FCSTD DOCUMENT  (FreeCAD 0.19.4R1_voidlinux)
Label: asm_clock_hands
License: All rights reserved
LicenseURL: http://en.wikipedia.org/wiki/All_rights_reserved
objects: App::Link×5, App::DocumentObjectGroup×3, PartDesign::CoordinateSystem×1, App::FeaturePython×1, App::Part×1
note: 1 computed .brp shape members not serialized (recipe doc carries the construction recipe); baked Part::Feature solids carry a one-line shape summary decoded from their .brp
EXTERNAL_REF file=clock_face.FCStd obj=LCS_tophole
EXTERNAL_REF file=clock_face.FCStd obj=Part
EXTERNAL_REF file=hand_alarm.FCStd obj=LCS_tophole
EXTERNAL_REF file=hand_alarm.FCStd obj=Part
EXTERNAL_REF file=hand_hour.FCStd obj=LCS_tophole
EXTERNAL_REF file=hand_hour.FCStd obj=Part
EXTERNAL_REF file=hand_minute.FCStd obj=LCS_tophole
EXTERNAL_REF file=hand_minute.FCStd obj=Part
EXTERNAL_REF file=hand_seconds.FCStd obj=LCS_topcenter
EXTERNAL_REF file=hand_seconds.FCStd obj=Part

FEATURE [App::DocumentObjectGroup] Parts
FEATURE [PartDesign::CoordinateSystem] LCS_Origin
  AttacherType = Attacher::AttachEngine3D
  MapMode = 2
  Support = -> [X_Axis]
FEATURE [App::DocumentObjectGroup] Constraints
FEATURE [App::FeaturePython] Variables  # WARN: FeaturePython — macro-defined, semantics opaque (R4)
  Type = App::PropertyContainer
FEATURE [App::DocumentObjectGroup] Configurations
FEATURE [App::Link] clock_face
  AttachedBy = #LCS_tophole
  AttachedTo = Parent Assembly#LCS_Origin
  LinkPlacement = pos=(0,0,0) rot=(0,0,-1;1.5708rad)
  LinkedObject = -> <external clock_face.FCStd>#Part
  Placement = pos=(0,0,0) rot=(0,0,-1;1.5708rad)
  SolverId = Asm4EE
  expr: Placement = LCS_Origin.Placement * AttachmentOffset * clock_face#LCS_tophole.Placement ^ -1
FEATURE [App::Link] hand_alarm
  AttachedBy = #LCS_tophole
  AttachedTo = clock_face#LCS_tophole
  AttachmentOffset = pos=(0,0,1.3) rot=(0,0,1;0rad)
  LinkPlacement = pos=(0,0,1.3) rot=(0,0,1;1.0472rad)
  LinkedObject = -> <external hand_alarm.FCStd>#Part
  Placement = pos=(0,0,1.3) rot=(0,0,1;1.0472rad)
  SolverId = Asm4EE
  expr: Placement = clock_face.Placement * clock_face#LCS_tophole.Placement * AttachmentOffset * hand_alarm#LCS_tophole.Placement ^ -1
FEATURE [App::Link] hand_hour
  AttachedBy = #LCS_tophole
  AttachedTo = clock_face#LCS_tophole
  AttachmentOffset = pos=(0,0,2.6) rot=(0,0,1;0rad)
  LinkPlacement = pos=(0,0,2.6) rot=(0,0,1;2.0944rad)
  LinkedObject = -> <external hand_hour.FCStd>#Part
  Placement = pos=(0,0,2.6) rot=(0,0,1;2.0944rad)
  SolverId = Asm4EE
  expr: Placement = clock_face.Placement * clock_face#LCS_tophole.Placement * AttachmentOffset * hand_hour#LCS_tophole.Placement ^ -1
FEATURE [App::Link] hand_minute
  AttachedBy = #LCS_tophole
  AttachedTo = clock_face#LCS_tophole
  AttachmentOffset = pos=(0,0,3.9) rot=(0,0,1;0rad)
  LinkPlacement = pos=(0,0,3.9) rot=(0,0,1;0.349066rad)
  LinkedObject = -> <external hand_minute.FCStd>#Part
  Placement = pos=(0,0,3.9) rot=(0,0,1;0.349066rad)
  SolverId = Asm4EE
  expr: Placement = clock_face.Placement * clock_face#LCS_tophole.Placement * AttachmentOffset * hand_minute#LCS_tophole.Placement ^ -1
FEATURE [App::Link] hand_seconds
  AttachedBy = #LCS_topcenter
  AttachedTo = clock_face#LCS_tophole
  AttachmentOffset = pos=(0,0,5.5) rot=(0,0,1;0rad)
  LinkPlacement = pos=(8e-16,-5e-16,4.1) rot=(0,0,1;0rad)
  LinkedObject = -> <external hand_seconds.FCStd>#Part
  Placement = pos=(8e-16,-5e-16,4.1) rot=(0,0,1;0rad)
  SolverId = Asm4EE
  expr: Placement = clock_face.Placement * clock_face#LCS_tophole.Placement * AttachmentOffset * hand_seconds#LCS_topcenter.Placement ^ -1
FEATURE [App::Part] Model
  Group = -> [LCS_Origin,Constraints,Variables,Configurations,clock_face,hand_alarm,hand_hour,hand_minute,hand_seconds]
  Origin = -> Origin
  Type = Assembly

RESOLVED EXTERNAL PARTS (link-assembly join: the EXTERNAL_REF files above that resolve inside this repo's crawl, each included once):
---- part clock_face.FCStd = doc fcstd_eb16558f8f3e ----
FCSTD DOCUMENT  (FreeCAD 0.19.4R1_voidlinux)
Label: clock_face
License: All rights reserved
LicenseURL: http://en.wikipedia.org/wiki/All_rights_reserved
objects: Sketcher::SketchObject×2, PartDesign::Pad×1, PartDesign::Pocket×1, PartDesign::Body×1, PartDesign::CoordinateSystem×1, App::Part×1
note: 8 computed .brp shape members not serialized (recipe doc carries the construction recipe); baked Part::Feature solids carry a one-line shape summary decoded from their .brp
EXTERNAL_REF file=master_animator.FCStd obj=Variables

FEATURE [Sketcher::SketchObject] Sketch
  FullyConstrained = true
  MapMode = 5
  Support = -> [XY_Plane001]
  sketch-geometry (8):
    g0: LineSegment StartX=-26 StartY=22 StartZ=0 EndX=-26 EndY=-22 EndZ=0
    g1: LineSegment StartX=26 StartY=22 StartZ=0 EndX=26 EndY=-22 EndZ=0
    g2: LineSegment StartX=-22 StartY=26 StartZ=0 EndX=22 EndY=26 EndZ=0
    g3: LineSegment StartX=-22 StartY=-26 StartZ=0 EndX=22 EndY=-26 EndZ=0
    g4: ArcOfCircle CenterX=-22 CenterY=22 CenterZ=0 NormalX=0 NormalY=0 NormalZ=1 AngleXU=0 Radius=4 StartAngle=1.57079 EndAngle=3.1416
    g5: ArcOfCircle CenterX=22 CenterY=22 CenterZ=0 NormalX=0 NormalY=0 NormalZ=1 AngleXU=0 Radius=4.00002 StartAngle=1.95399e-08 EndAngle=1.5708
    g6: ArcOfCircle CenterX=22 CenterY=-22 CenterZ=0 NormalX=0 NormalY=0 NormalZ=1 AngleXU=0 Radius=4.00002 StartAngle=4.71239 EndAngle=6.28319
    g7: ArcOfCircle CenterX=-22 CenterY=-22 CenterZ=0 NormalX=0 NormalY=0 NormalZ=1 AngleXU=0 Radius=4.00002 StartAngle=3.14159 EndAngle=4.71239
  constraints (22):
    c: Coincident(g4,g2)
    c: Coincident(g4,g0)
    c: Coincident(g5,g1)
    c: Coincident(g5,g2)
    c: Coincident(g6,g1)
    c: Coincident(g6,g3)
    c: Coincident(g7,g0)
    c: Coincident(g7,g3)
    c: Symmetric(g1,g0,g-2)
    c: Symmetric(g2,g2,g-2)
    c: Symmetric(g0,g0,g-1)
    c: Symmetric(g2,g3,g-1)
    c: Symmetric(g3,g2,g-1)
    c: Symmetric(g1,g0,g-1)
    c: Tangent(g4,g2)
    c: Tangent(g4,g0)
    c: Tangent(g0,g7)
    c: Tangent(g3,g6)
    c: Tangent(g1,g5)
    c: DistanceY(g3,g2) = 52
    c: Equal(g0,g2)
    c: Radius(g4) = 4
FEATURE [PartDesign::Pad] Pad
  Direction = (1,1,1)
  Length = 1
  Length2 = 100
  Profile = -> Sketch
  Reversed = true
  Type = 0
FEATURE [Sketcher::SketchObject] Sketch001
  FullyConstrained = true
  MapMode = 5
  Support = -> [Pad]
  sketch-geometry (1):
    g0: Circle CenterX=0 CenterY=0 CenterZ=0 NormalX=0 NormalY=0 NormalZ=1 AngleXU=0 Radius=3
  constraints (2):
    c: Coincident(g0,g-1)
    c: Radius(g0) = 3
FEATURE [PartDesign::Pocket] Pocket
  BaseFeature = -> Pad
  Length = 5
  Length2 = 100
  Profile = -> Sketch001
  Type = 1
FEATURE [PartDesign::Body] Body
  Group = -> [Sketch,Pad,Sketch001,Pocket]
  Origin = -> Origin001
  Tip = -> Pocket
FEATURE [PartDesign::CoordinateSystem] LCS_tophole
  AttacherType = Attacher::AttachEngine3D
  MapMode = 11
  Placement = pos=(0,0,0) rot=(0,0,1;1.5708rad)
  Support = -> [Pocket]
  expr: .AttachmentOffset.Base.z = -master_animator#Variables.explode * 3
FEATURE [App::Part] Part  label="clock_face"
  Group = -> [LCS_tophole,Body]
  Origin = -> Origin
---- part hand_alarm.FCStd = doc fcstd_c77f37d60b10 ----
FCSTD DOCUMENT  (FreeCAD 0.19.4R1_voidlinux)
Label: hand_alarm
License: All rights reserved
LicenseURL: http://en.wikipedia.org/wiki/All_rights_reserved
objects: Sketcher::SketchObject×2, PartDesign::Revolution×1, PartDesign::Pocket×1, PartDesign::Body×1, PartDesign::CoordinateSystem×1, App::Part×1
note: 8 computed .brp shape members not serialized (recipe doc carries the construction recipe); baked Part::Feature solids carry a one-line shape summary decoded from their .brp
EXTERNAL_REF file=master_animator.FCStd obj=Variables

FEATURE [Sketcher::SketchObject] Sketch
  FullyConstrained = true
  MapMode = 5
  Placement = pos=(0,0,0) rot=(0.57735,0.57735,0.57735;2.0944rad)
  Support = -> [YZ_Plane001]
  sketch-geometry (6):
    g0: LineSegment StartX=-14 StartY=0 StartZ=0 EndX=-14 EndY=-1 EndZ=0
    g1: LineSegment StartX=-14 StartY=-1 StartZ=0 EndX=-2.8 EndY=-1 EndZ=0
    g2: LineSegment StartX=-2.8 StartY=-1 StartZ=0 EndX=-2.8 EndY=-5 EndZ=0
    g3: LineSegment StartX=-2.8 StartY=-5 StartZ=0 EndX=-2.3 EndY=-5 EndZ=0
    g4: LineSegment StartX=-2.3 StartY=-5 StartZ=0 EndX=-2.3 EndY=0 EndZ=0
    g5: LineSegment StartX=-14 StartY=0 StartZ=0 EndX=-2.3 EndY=0 EndZ=0
  constraints (18):
    c: PointOnObject(g0,g-1)
    c: Vertical(g0)
    c: Coincident(g1,g0)
    c: Horizontal(g1)
    c: Coincident(g2,g1)
    c: Vertical(g2)
    c: Coincident(g3,g2)
    c: Horizontal(g3)
    c: Coincident(g4,g3)
    c: Vertical(g4)
    c: PointOnObject(g4,g-1)
    c: Coincident(g5,g0)
    c: Coincident(g5,g4)
    c: Distance(g3) = 0.5
    c: DistanceX(g-2,g2) = -2.8
    c: DistanceX(g-2,g0) = -14
    c: Distance(g4) = 5
    c: Distance(g0) = 1
FEATURE [PartDesign::Revolution] Revolution
  Angle = 360
  Axis = (-2e-16,3e-16,1)
  Base = (0,0,0)
  Placement = pos=(0,0,0) rot=(0.57735,0.57735,0.57735;2.0944rad)
  Profile = -> Sketch
  ReferenceAxis = -> Sketch [V_Axis]
FEATURE [Sketcher::SketchObject] Sketch001
  ExternalGeometry = -> [Revolution]
  FullyConstrained = true
  MapMode = 5
  Placement = pos=(0,0,2.3e-15) rot=(0,0,-1;1.5708rad)
  Support = -> [Revolution]
  sketch-geometry (6):
    g0: LineSegment StartX=-13.9943 StartY=0.4 StartZ=0 EndX=-3.4641 EndY=0.5 EndZ=0
    g1: LineSegment StartX=-3.4641 StartY=-0.5 StartZ=0 EndX=-13.9943 EndY=-0.4 EndZ=0
    g2: ArcOfCircle CenterX=-2e-16 CenterY=9e-15 CenterZ=0 NormalX=0 NormalY=0 NormalZ=1 AngleXU=0 Radius=14 StartAngle=3.17017 EndAngle=9.3962
    g3: ArcOfCircle CenterX=-2e-16 CenterY=9e-15 CenterZ=0 NormalX=0 NormalY=0 NormalZ=1 AngleXU=0 Radius=3.5 StartAngle=3.28494 EndAngle=9.28143
    g4: LineSegment StartX=-3.4641 StartY=0.5 StartZ=0 EndX=-3.4641 EndY=0 EndZ=0
    g5: LineSegment StartX=-3.4641 StartY=0 StartZ=0 EndX=-3.4641 EndY=-0.5 EndZ=0
  constraints (17):
    c: PointOnObject(g0,g-3)
    c: Symmetric(g0,g1,g-1)
    c: DistanceY(g1,g0) = 1
    c: Coincident(g2,g0)
    c: Coincident(g2,g1)
    c: Coincident(g3,g2)
    c: Coincident(g3,g0)
    c: Radius(g3) = 3.5
    c: Equal(g2,g-3)
    c: DistanceY(g1,g0) = 0.8
    c: Coincident(g3,g1)
    c: Coincident(g4,g0)
    c: PointOnObject(g4,g-1)
    c: Vertical(g4)
    c: Coincident(g5,g4)
    c: Coincident(g5,g1)
    c: Vertical(g5)
FEATURE [PartDesign::Pocket] Pocket
  BaseFeature = -> Revolution
  Length = 5
  Length2 = 100
  Placement = pos=(0,0,0) rot=(0.57735,0.57735,0.57735;2.0944rad)
  Profile = -> Sketch001
  Type = 1
FEATURE [PartDesign::Body] Body
  Group = -> [Sketch,Revolution,Sketch001,Pocket]
  Origin = -> Origin001
  Tip = -> Pocket
FEATURE [PartDesign::CoordinateSystem] LCS_tophole
  AttacherType = Attacher::AttachEngine3D
  AttachmentOffset = pos=(0,0,0) rot=(0,0,-1;1.0472rad)
  MapMode = 11
  Placement = pos=(0,0,4e-16) rot=(0,0,-1;1.0472rad)
  Support = -> [Pocket]
  expr: .AttachmentOffset.Base.z = -master_animator#Variables.explode * 4
FEATURE [App::Part] Part  label="hand_alarm"
  Group = -> [LCS_tophole,Body]
  Origin = -> Origin
---- part hand_hour.FCStd = doc fcstd_4f2025e096bf ----
FCSTD DOCUMENT  (FreeCAD 0.19.4R1_voidlinux)
Label: hand_hour
License: All rights reserved
LicenseURL: http://en.wikipedia.org/wiki/All_rights_reserved
objects: Sketcher::SketchObject×3, PartDesign::Revolution×1, PartDesign::Pad×1, PartDesign::Pocket×1, PartDesign::Body×1, PartDesign::CoordinateSystem×1, App::Part×1
note: 11 computed .brp shape members not serialized (recipe doc carries the construction recipe); baked Part::Feature solids carry a one-line shape summary decoded from their .brp
EXTERNAL_REF file=master_animator.FCStd obj=Variables

FEATURE [Sketcher::SketchObject] Sketch
  FullyConstrained = true
  MapMode = 5
  Placement = pos=(0,0,0) rot=(0.57735,0.57735,0.57735;2.0944rad)
  Support = -> [YZ_Plane001]
  sketch-geometry (6):
    g0: LineSegment StartX=-3.3 StartY=0 StartZ=0 EndX=-1.7 EndY=0 EndZ=0
    g1: LineSegment StartX=-1.7 StartY=0 StartZ=0 EndX=-1.7 EndY=-7 EndZ=0
    g2: LineSegment StartX=-1.7 StartY=-7 StartZ=0 EndX=-2.2 EndY=-7 EndZ=0
    g3: LineSegment StartX=-2.2 StartY=-7 StartZ=0 EndX=-2.2 EndY=-1 EndZ=0
    g4: LineSegment StartX=-2.2 StartY=-1 StartZ=0 EndX=-3.3 EndY=-1 EndZ=0
    g5: LineSegment StartX=-3.3 StartY=0 StartZ=0 EndX=-3.3 EndY=-1 EndZ=0
  constraints (18):
    c: PointOnObject(g0,g-1)
    c: PointOnObject(g0,g-1)
    c: Coincident(g1,g0)
    c: Vertical(g1)
    c: Coincident(g2,g1)
    c: Horizontal(g2)
    c: Coincident(g3,g2)
    c: Vertical(g3)
    c: Coincident(g4,g3)
    c: Horizontal(g4)
    c: Coincident(g5,g0)
    c: Coincident(g5,g4)
    c: Vertical(g5)
    c: Distance(g5) = 1
    c: Distance(g2) = 0.5
    c: Distance(g1) = 7
    c: DistanceX(g0,g-1) = 3.3
    c: DistanceX(g2,g-1) = 2.2
FEATURE [PartDesign::Revolution] Revolution
  Angle = 360
  Axis = (-2e-16,3e-16,1)
  Base = (0,0,0)
  Placement = pos=(0,0,0) rot=(0.57735,0.57735,0.57735;2.0944rad)
  Profile = -> Sketch
  ReferenceAxis = -> Sketch [V_Axis]
FEATURE [Sketcher::SketchObject] Sketch001
  ExternalGeometry = -> [Revolution]
  FullyConstrained = true
  MapMode = 5
  Placement = pos=(0,0,5e-16) rot=(0,0,-1;1.5708rad)
  Support = -> [Revolution]
  sketch-geometry (5):
    g0: LineSegment StartX=3.10232 StartY=1.125 StartZ=0 EndX=3.10232 EndY=-1.125 EndZ=0
    g1: LineSegment StartX=3.10232 StartY=1.125 StartZ=0 EndX=17.009 EndY=1 EndZ=0
    g2: LineSegment StartX=3.10232 StartY=-1.125 StartZ=0 EndX=17.009 EndY=-1 EndZ=0
    g3: ArcOfCircle CenterX=17 CenterY=0 CenterZ=0 NormalX=0 NormalY=0 NormalZ=1 AngleXU=0 Radius=1.00004 StartAngle=4.72138 EndAngle=7.84499
    g4: GeomPoint X=16 Y=0 Z=0
  constraints (13):
    c: PointOnObject(g0,g-3)
    c: Symmetric(g0,g0,g-1)
    c: Coincident(g1,g0)
    c: Coincident(g2,g0)
    c: Symmetric(g1,g2,g-1)
    c: DistanceY(g2,g1) = 2
    c: DistanceY(g0,g0) = 2.25
    c: Coincident(g3,g1)
    c: Coincident(g3,g2)
    c: Tangent(g3,g1)
    c: PointOnObject(g4,g3)
    c: PointOnObject(g4,g-1)
    c: Distance(g-1,g4) = 16
FEATURE [PartDesign::Pad] Pad
  BaseFeature = -> Revolution
  Direction = (1,1,1)
  Length = 1
  Length2 = 100
  Placement = pos=(0,0,0) rot=(0.57735,0.57735,0.57735;2.0944rad)
  Profile = -> Sketch001
  Reversed = true
  Type = 0
FEATURE [Sketcher::SketchObject] Sketch002
  ExternalGeometry = -> [Pad]
  FullyConstrained = true
  MapMode = 5
  Placement = pos=(0,0,5e-16) rot=(0,0,-1;1.5708rad)
  Support = -> [Pad]
  sketch-geometry (7):
    g0: ArcOfCircle CenterX=11.5751 CenterY=0 CenterZ=0 NormalX=0 NormalY=0 NormalZ=1 AngleXU=0 Radius=0.575 StartAngle=1.5708 EndAngle=4.71239
    g1: ArcOfCircle CenterX=15.4251 CenterY=0 CenterZ=0 NormalX=0 NormalY=0 NormalZ=1 AngleXU=0 Radius=0.575 StartAngle=4.71239 EndAngle=7.85398
    g2: LineSegment StartX=11.5751 StartY=-0.575 StartZ=0 EndX=15.4251 EndY=-0.575 EndZ=0
    g3: LineSegment StartX=11.5751 StartY=0.575 StartZ=0 EndX=15.4251 EndY=0.575 EndZ=0
    g4: GeomPoint X=11.0001 Y=0 Z=0
    g5: GeomPoint X=16.0001 Y=0 Z=0
    g6: GeomPoint X=18.0001 Y=0 Z=0
  constraints (16):
    c: Tangent(g0,g3) = 1.5708
    c: Tangent(g0,g2) = -1.5708
    c: Tangent(g2,g1) = -1.5708
    c: Tangent(g3,g1) = 1.5708
    c: Horizontal(g2)
    c: Equal(g0,g1)
    c: PointOnObject(g0,g-1)
    c: PointOnObject(g4,g0)
    c: PointOnObject(g5,g1)
    c: PointOnObject(g4,g-1)
    c: PointOnObject(g5,g-1)
    c: Distance(g4,g5) = 5
    c: Distance(g0,g0) = 1.15
    c: PointOnObject(g6,g-3)
    c: PointOnObject(g6,g-1)
    c: Distance(g5,g6) = 2
FEATURE [PartDesign::Pocket] Pocket
  BaseFeature = -> Pad
  Length = 0.1
  Length2 = 100
  Placement = pos=(0,0,0) rot=(0.57735,0.57735,0.57735;2.0944rad)
  Profile = -> Sketch002
  Type = 0
FEATURE [PartDesign::Body] Body
  Group = -> [Sketch,Revolution,Sketch001,Pad,Sketch002,Pocket]
  Origin = -> Origin001
  Tip = -> Pocket
FEATURE [PartDesign::CoordinateSystem] LCS_tophole
  AttacherType = Attacher::AttachEngine3D
  AttachmentOffset = pos=(0,0,0) rot=(0,0,-1;2.0944rad)
  MapMode = 11
  Placement = pos=(0,0,3e-16) rot=(0,0,-1;2.0944rad)
  Support = -> [Pocket]
  expr: .AttachmentOffset.Base.z = -master_animator#Variables.explode * 5
FEATURE [App::Part] Part  label="hand_hour"
  Group = -> [LCS_tophole,Body]
  Origin = -> Origin
---- part hand_minute.FCStd = doc fcstd_699d8df3e5ea ----
FCSTD DOCUMENT  (FreeCAD 0.19.4R1_voidlinux)
Label: hand_minute
License: All rights reserved
LicenseURL: http://en.wikipedia.org/wiki/All_rights_reserved
objects: Sketcher::SketchObject×3, PartDesign::Revolution×1, PartDesign::Pad×1, PartDesign::Pocket×1, PartDesign::Body×1, PartDesign::CoordinateSystem×1, App::Part×1
note: 11 computed .brp shape members not serialized (recipe doc carries the construction recipe); baked Part::Feature solids carry a one-line shape summary decoded from their .brp
EXTERNAL_REF file=master_animator.FCStd obj=Variables

FEATURE [Sketcher::SketchObject] Sketch
  FullyConstrained = true
  MapMode = 5
  Placement = pos=(0,0,0) rot=(0.57735,0.57735,0.57735;2.0944rad)
  Support = -> [YZ_Plane001]
  sketch-geometry (6):
    g0: LineSegment StartX=-3 StartY=0 StartZ=0 EndX=-1.1 EndY=0 EndZ=0
    g1: LineSegment StartX=-1.1 StartY=0 StartZ=0 EndX=-1.1 EndY=-9 EndZ=0
    g2: LineSegment StartX=-1.1 StartY=-9 StartZ=0 EndX=-1.6 EndY=-9 EndZ=0
    g3: LineSegment StartX=-1.6 StartY=-9 StartZ=0 EndX=-1.6 EndY=-1 EndZ=0
    g4: LineSegment StartX=-1.6 StartY=-1 StartZ=0 EndX=-3 EndY=-1 EndZ=0
    g5: LineSegment StartX=-3 StartY=-1 StartZ=0 EndX=-3 EndY=0 EndZ=0
  constraints (18):
    c: PointOnObject(g0,g-1)
    c: PointOnObject(g0,g-1)
    c: Coincident(g1,g0)
    c: Vertical(g1)
    c: Coincident(g2,g1)
    c: Horizontal(g2)
    c: Coincident(g3,g2)
    c: Vertical(g3)
    c: Coincident(g4,g3)
    c: Horizontal(g4)
    c: Coincident(g5,g4)
    c: Coincident(g5,g0)
    c: Vertical(g5)
    c: Distance(g2) = 0.5
    c: Distance(g0,g1) = 9
    c: Distance(g5) = 1
    c: Distance(g-1,g0) = 3
    c: DistanceX(g-2,g2) = -1.6
FEATURE [PartDesign::Revolution] Revolution
  Angle = 360
  Axis = (-2e-16,3e-16,1)
  Base = (0,0,0)
  Placement = pos=(0,0,0) rot=(0.57735,0.57735,0.57735;2.0944rad)
  Profile = -> Sketch
  ReferenceAxis = -> Sketch [V_Axis]
FEATURE [Sketcher::SketchObject] Sketch001
  ExternalGeometry = -> [Revolution]
  FullyConstrained = true
  MapMode = 5
  Placement = pos=(0,0,5e-16) rot=(0,0,-1;1.5708rad)
  Support = -> [Revolution]
  sketch-geometry (5):
    g0: LineSegment StartX=2.78107 StartY=1.125 StartZ=0 EndX=2.78107 EndY=-1.125 EndZ=0
    g1: LineSegment StartX=2.78107 StartY=1.125 StartZ=0 EndX=20.507 EndY=1 EndZ=0
    g2: LineSegment StartX=2.78107 StartY=-1.125 StartZ=0 EndX=20.507 EndY=-1 EndZ=0
    g3: ArcOfCircle CenterX=20.5 CenterY=0 CenterZ=0 NormalX=0 NormalY=0 NormalZ=1 AngleXU=0 Radius=1.00002 StartAngle=4.71944 EndAngle=7.84694
    g4: GeomPoint X=21.5 Y=0 Z=0
  constraints (13):
    c: PointOnObject(g0,g-3)
    c: Symmetric(g0,g0,g-1)
    c: Distance(g0) = 2.25
    c: Coincident(g1,g0)
    c: Coincident(g2,g0)
    c: Symmetric(g1,g2,g-1)
    c: Distance(g1,g2) = 2
    c: Coincident(g3,g1)
    c: Coincident(g3,g2)
    c: Tangent(g3,g1)
    c: PointOnObject(g4,g3)
    c: PointOnObject(g4,g-1)
    c: Distance(g-1,g4) = 21.5
FEATURE [PartDesign::Pad] Pad
  BaseFeature = -> Revolution
  Direction = (1,1,1)
  Length = 1
  Length2 = 100
  Placement = pos=(0,0,0) rot=(0.57735,0.57735,0.57735;2.0944rad)
  Profile = -> Sketch001
  Reversed = true
  Type = 0
FEATURE [Sketcher::SketchObject] Sketch002
  ExternalGeometry = -> [Pad]
  FullyConstrained = true
  MapMode = 5
  Placement = pos=(0,0,5e-16) rot=(0,0,-1;1.5708rad)
  Support = -> [Pad]
  sketch-geometry (7):
    g0: ArcOfCircle CenterX=12 CenterY=0 CenterZ=0 NormalX=0 NormalY=0 NormalZ=1 AngleXU=0 Radius=0.5 StartAngle=1.5708 EndAngle=4.71239
    g1: ArcOfCircle CenterX=18 CenterY=0 CenterZ=0 NormalX=0 NormalY=0 NormalZ=1 AngleXU=0 Radius=0.5 StartAngle=4.71239 EndAngle=7.85398
    g2: LineSegment StartX=12 StartY=-0.5 StartZ=0 EndX=18 EndY=-0.5 EndZ=0
    g3: LineSegment StartX=12 StartY=0.5 StartZ=0 EndX=18 EndY=0.5 EndZ=0
    g4: GeomPoint X=21.5 Y=0 Z=0
    g5: GeomPoint X=18.5 Y=0 Z=0
    g6: GeomPoint X=11.5 Y=0 Z=0
  constraints (16):
    c: Tangent(g0,g3) = 1.5708
    c: Tangent(g0,g2) = -1.5708
    c: Tangent(g2,g1) = -1.5708
    c: Tangent(g3,g1) = 1.5708
    c: Horizontal(g2)
    c: Equal(g0,g1)
    c: PointOnObject(g0,g-1)
    c: PointOnObject(g4,g-3)
    c: PointOnObject(g4,g-1)
    c: PointOnObject(g5,g1)
    c: PointOnObject(g5,g-1)
    c: Distance(g5,g4) = 3
    c: PointOnObject(g6,g0)
    c: PointOnObject(g6,g-1)
    c: Distance(g6,g5) = 7
    c: Distance(g0,g0) = 1
FEATURE [PartDesign::Pocket] Pocket
  BaseFeature = -> Pad
  Length = 0.1
  Length2 = 100
  Placement = pos=(0,0,0) rot=(0.57735,0.57735,0.57735;2.0944rad)
  Profile = -> Sketch002
  Type = 0
FEATURE [PartDesign::Body] Body
  Group = -> [Sketch,Revolution,Sketch001,Pad,Sketch002,Pocket]
  Origin = -> Origin001
  Tip = -> Pocket
FEATURE [PartDesign::CoordinateSystem] LCS_tophole
  AttacherType = Attacher::AttachEngine3D
  AttachmentOffset = pos=(0,0,0) rot=(0,0,-1;0.349066rad)
  MapMode = 11
  Placement = pos=(0,0,2e-16) rot=(0,0,-1;0.349066rad)
  Support = -> [Pocket]
  expr: .AttachmentOffset.Base.z = -master_animator#Variables.explode * 6
FEATURE [App::Part] Part  label="hand_minute"
  Group = -> [LCS_tophole,Body]
  Origin = -> Origin
---- part hand_seconds.FCStd = doc fcstd_aaa8d5bff472 ----
FCSTD DOCUMENT  (FreeCAD 0.19.4R1_voidlinux)
Label: hand_seconds
License: All rights reserved
LicenseURL: http://en.wikipedia.org/wiki/All_rights_reserved
objects: Sketcher::SketchObject×3, PartDesign::Body×2, PartDesign::AdditiveLoft×1, PartDesign::Revolution×1, Part::Fuse×1, PartDesign::CoordinateSystem×1, App::Part×1
note: 11 computed .brp shape members not serialized (recipe doc carries the construction recipe); baked Part::Feature solids carry a one-line shape summary decoded from their .brp
EXTERNAL_REF file=master_animator.FCStd obj=Variables

FEATURE [Sketcher::SketchObject] Sketch  label="fat_end"
  FullyConstrained = true
  MapMode = 5
  Placement = pos=(0,0,0) rot=(1,0,0;1.5708rad)
  Support = -> [XZ_Plane002]
  sketch-geometry (5):
    g0: LineSegment StartX=-0.5 StartY=0 StartZ=0 EndX=0.5 EndY=0 EndZ=0
    g1: LineSegment StartX=-0.5 StartY=0 StartZ=0 EndX=-0.441963 EndY=0.329146 EndZ=0
    g2: LineSegment StartX=0.5 StartY=0 StartZ=0 EndX=0.441963 EndY=0.329146 EndZ=0
    g3: ArcOfCircle CenterX=0 CenterY=0.25122 CenterZ=0 NormalX=0 NormalY=0 NormalZ=1 AngleXU=0 Radius=0.44878 StartAngle=0.174523 EndAngle=2.96707
    g4: GeomPoint X=0 Y=0.7 Z=0
  constraints (13):
    c: PointOnObject(g0,g-1)
    c: Coincident(g1,g0)
    c: Coincident(g2,g0)
    c: Coincident(g3,g1)
    c: Coincident(g3,g2)
    c: Symmetric(g0,g0,g-2)
    c: Symmetric(g2,g1,g-2)
    c: Tangent(g3,g1)
    c: PointOnObject(g4,g3)
    c: PointOnObject(g4,g-2)
    c: DistanceY(g0,g4) = 0.7
    c: Distance(g0) = 1
    c: Angle(g-1,g1) = 1.39626
FEATURE [Sketcher::SketchObject] Sketch001  label="thin_end"
  AttachmentOffset = pos=(0,0,-30) rot=(0,0,1;0rad)
  FullyConstrained = true
  MapMode = 5
  Placement = pos=(0,30,6.7e-15) rot=(1,0,0;1.5708rad)
  Support = -> [XZ_Plane002]
  sketch-geometry (5):
    g0: LineSegment StartX=-0.35 StartY=0 StartZ=0 EndX=0.35 EndY=0 EndZ=0
    g1: LineSegment StartX=-0.35 StartY=0 StartZ=0 EndX=-0.286609 EndY=0.359509 EndZ=0
    g2: LineSegment StartX=0.35 StartY=0 StartZ=0 EndX=0.286609 EndY=0.359509 EndZ=0
    g3: ArcOfCircle CenterX=0 CenterY=0.308969 CenterZ=0 NormalX=0 NormalY=0 NormalZ=1 AngleXU=0 Radius=0.291031 StartAngle=0.174544 EndAngle=2.96705
    g4: GeomPoint X=0 Y=0.6 Z=0
  constraints (13):
    c: PointOnObject(g0,g-1)
    c: Coincident(g1,g0)
    c: Coincident(g2,g0)
    c: Coincident(g3,g1)
    c: Coincident(g3,g2)
    c: Symmetric(g0,g0,g-2)
    c: Symmetric(g2,g1,g-2)
    c: Tangent(g3,g1)
    c: PointOnObject(g4,g3)
    c: PointOnObject(g4,g-2)
    c: DistanceY(g0,g4) = 0.6
    c: Distance(g0) = 0.7
    c: Angle(g-1,g1) = 1.39626
FEATURE [PartDesign::AdditiveLoft] AdditiveLoft
  Closed = false
  Placement = pos=(0,0,0) rot=(1,0,0;1.5708rad)
  Profile = -> Sketch
  Ruled = false
  Sections = -> [Sketch001]
FEATURE [PartDesign::Body] Body001  label="hand"
  Group = -> [Sketch,Sketch001,AdditiveLoft]
  Origin = -> Origin002
  Placement = pos=(0,-7.5,0.5) rot=(0,0,1;0rad)
  Tip = -> AdditiveLoft
FEATURE [Sketcher::SketchObject] Sketch002
  FullyConstrained = true
  MapMode = 5
  Placement = pos=(0,0,0) rot=(0.57735,0.57735,0.57735;2.0944rad)
  Support = -> [YZ_Plane001]
  sketch-geometry (32):
    g0: LineSegment StartX=-2.5 StartY=0 StartZ=0 EndX=-2.37675 EndY=1.40872 EndZ=0
    g1: LineSegment StartX=-2.5 StartY=0 StartZ=0 EndX=-1 EndY=0 EndZ=0
    g2: LineSegment StartX=-1 StartY=0 StartZ=0 EndX=-1 EndY=-10 EndZ=0
    g3: LineSegment StartX=-1 StartY=-10 StartZ=0 EndX=-3.26e-14 EndY=-10 EndZ=0
    g4: LineSegment StartX=-3.26e-14 StartY=-10 StartZ=0 EndX=-5.356e-13 EndY=1.4 EndZ=0
    g5: LineSegment StartX=-2.27713 StartY=1.5 StartZ=0 EndX=-2.10875 EndY=1.5 EndZ=0
    g6: LineSegment StartX=-2.10875 StartY=1.5 StartZ=0 EndX=-2.1 EndY=1.4 EndZ=0
    g7: LineSegment StartX=-2.1 StartY=1.4 StartZ=0 EndX=-2.025 EndY=1.4 EndZ=0
    g8: ArcOfCircle CenterX=-1.96125 CenterY=1.4 CenterZ=0 NormalX=0 NormalY=0 NormalZ=1 AngleXU=0 Radius=0.06375 StartAngle=-1.803e-13 EndAngle=3.14159
    g9: LineSegment StartX=-2.1 StartY=1.4 StartZ=0 EndX=-5.356e-13 EndY=1.4 EndZ=0
    g10: LineSegment StartX=-1.8975 StartY=1.4 StartZ=0 EndX=-1.8225 EndY=1.4 EndZ=0
    g11: LineSegment StartX=-1.695 StartY=1.4 StartZ=0 EndX=-1.62 EndY=1.4 EndZ=0
    g12: LineSegment StartX=-1.4925 StartY=1.4 StartZ=0 EndX=-1.4175 EndY=1.4 EndZ=0
    g13: LineSegment StartX=-1.0875 StartY=1.4 StartZ=0 EndX=-1.0125 EndY=1.4 EndZ=0
    g14: LineSegment StartX=-0.885 StartY=1.4 StartZ=0 EndX=-0.81 EndY=1.4 EndZ=0
    g15: LineSegment StartX=-0.6825 StartY=1.4 StartZ=0 EndX=-0.6075 EndY=1.4 EndZ=0
    g16: LineSegment StartX=-0.48 StartY=1.4 StartZ=0 EndX=-0.405 EndY=1.4 EndZ=0
    g17: LineSegment StartX=-0.2775 StartY=1.4 StartZ=0 EndX=-0.2025 EndY=1.4 EndZ=0
    g18: LineSegment StartX=-0.075 StartY=1.4 StartZ=0 EndX=-5.356e-13 EndY=1.4 EndZ=0
    g19: LineSegment StartX=-1.29 StartY=1.4 StartZ=0 EndX=-1.215 EndY=1.4 EndZ=0
    g20: ArcOfCircle CenterX=-1.75875 CenterY=1.4 CenterZ=0 NormalX=0 NormalY=0 NormalZ=1 AngleXU=0 Radius=0.06375 StartAngle=-3.473e-13 EndAngle=3.14159
    g21: ArcOfCircle CenterX=-1.55625 CenterY=1.4 CenterZ=0 NormalX=0 NormalY=0 NormalZ=1 AngleXU=0 Radius=0.06375 StartAngle=-3.082e-13 EndAngle=3.14159
    g22: ArcOfCircle CenterX=-1.35375 CenterY=1.4 CenterZ=0 NormalX=0 NormalY=0 NormalZ=1 AngleXU=0 Radius=0.06375 StartAngle=-2.673e-13 EndAngle=3.14159
    g23: ArcOfCircle CenterX=-1.15125 CenterY=1.4 CenterZ=0 NormalX=0 NormalY=0 NormalZ=1 AngleXU=0 Radius=0.06375 StartAngle=-2.292e-13 EndAngle=3.14159
    g24: ArcOfCircle CenterX=-0.94875 CenterY=1.4 CenterZ=0 NormalX=0 NormalY=0 NormalZ=1 AngleXU=0 Radius=0.06375 StartAngle=-1.883e-13 EndAngle=3.14159
    g25: ArcOfCircle CenterX=-0.74625 CenterY=1.4 CenterZ=0 NormalX=0 NormalY=0 NormalZ=1 AngleXU=0 Radius=0.06375 StartAngle=-1.439e-13 EndAngle=3.14159
    g26: ArcOfCircle CenterX=-0.54375 CenterY=1.4 CenterZ=0 NormalX=0 NormalY=0 NormalZ=1 AngleXU=0 Radius=0.06375 StartAngle=-1.084e-13 EndAngle=3.14159
    g27: ArcOfCircle CenterX=-0.34125 CenterY=1.4 CenterZ=0 NormalX=0 NormalY=0 NormalZ=1 AngleXU=0 Radius=0.06375 StartAngle=-6.93e-14 EndAngle=3.14159
    g28: ArcOfCircle CenterX=-0.13875 CenterY=1.4 CenterZ=0 NormalX=0 NormalY=0 NormalZ=1 AngleXU=0 Radius=0.06375 StartAngle=-3.02e-14 EndAngle=3.14159
    g29: LineSegment StartX=-2.1 StartY=1.4 StartZ=0 EndX=-5.356e-13 EndY=1.4 EndZ=0
    g30: LineSegment StartX=-2.1 StartY=1.4 StartZ=0 EndX=-2.1 EndY=1.4 EndZ=0
    g31: ArcOfCircle CenterX=-2.27713 CenterY=1.4 CenterZ=0 NormalX=0 NormalY=0 NormalZ=1 AngleXU=0 Radius=0.1 StartAngle=1.5708 EndAngle=3.05433
  constraints (103):
    c: PointOnObject(g0,g-1)
    c: Coincident(g1,g0)
    c: PointOnObject(g1,g-1)
    c: Coincident(g2,g1)
    c: Vertical(g2)
    c: Coincident(g3,g2)
    c: PointOnObject(g3,g-2)
    c: Horizontal(g3)
    c: Coincident(g4,g3)
    c: PointOnObject(g4,g-2)
    c: Distance(g3) = 1
    c: Distance(g2) = 10
    c: Horizontal(g5)
    c: Coincident(g6,g5)
    c: Distance(g0,g4) = 2.5
    c: Coincident(g7,g6)
    c: Horizontal(g7)
    c: DistanceX(g0,g6) = 0.4
    c: Angle(g0,g-2) = 0.0872665
    c: Angle(g4,g6) = 0.0872665
    c: DistanceY(g6,g5) = 0.1
    c: Coincident(g8,g7)
    c: Coincident(g9,g6)
    c: Horizontal(g9)
    c: PointOnObject(g8,g9)
    c: Coincident(g10,g8)
    c: PointOnObject(g10,g9)
    c: PointOnObject(g11,g9)
    c: PointOnObject(g11,g9)
    c: PointOnObject(g12,g9)
    c: PointOnObject(g12,g9)
    c: PointOnObject(g13,g9)
    c: PointOnObject(g13,g9)
    c: PointOnObject(g14,g9)
    c: PointOnObject(g14,g9)
    c: PointOnObject(g15,g9)
    c: PointOnObject(g15,g9)
    c: PointOnObject(g16,g9)
    c: PointOnObject(g16,g9)
    c: PointOnObject(g17,g9)
    c: PointOnObject(g17,g9)
    c: PointOnObject(g18,g9)
    c: Equal(g7,g10)
    c: Equal(g10,g11)
    c: Equal(g11,g12)
    c: Equal(g12,g13)
    c: Equal(g13,g14)
    c: Equal(g14,g15)
    c: Equal(g15,g16)
    c: Equal(g16,g17)
    c: Equal(g17,g18)
    c: Distance(g7) = 0.075
    c: PointOnObject(g19,g9)
    c: PointOnObject(g19,g9)
    c: Equal(g19,g10)
    c: Coincident(g20,g10)
    c: Coincident(g20,g11)
    c: Coincident(g21,g11)
    c: Coincident(g21,g12)
    c: Coincident(g22,g12)
    c: Coincident(g22,g19)
    c: Coincident(g23,g19)
    c: Coincident(g23,g13)
    c: Coincident(g24,g13)
    c: Coincident(g24,g14)
    c: Coincident(g25,g14)
    c: Coincident(g25,g15)
    c: Coincident(g26,g15)
    c: Coincident(g26,g16)
    c: Coincident(g27,g16)
    c: Coincident(g27,g17)
    c: Coincident(g28,g17)
    c: Coincident(g28,g18)
    c: Coincident(g30,g6)
    c: Coincident(g30,g29)
    c: Vertical(g30)
    c: PointOnObject(g8,g29)
    c: PointOnObject(g20,g29)
    c: PointOnObject(g21,g29)
    c: PointOnObject(g22,g29)
    c: PointOnObject(g23,g29)
    c: PointOnObject(g24,g29)
    c: PointOnObject(g25,g29)
    c: PointOnObject(g26,g29)
    c: PointOnObject(g27,g29)
    c: PointOnObject(g28,g29)
    c: Coincident(g18,g9)
    c: Equal(g8,g20)
    c: Equal(g20,g21)
    c: Equal(g21,g22)
    c: Equal(g22,g23)
    c: Equal(g23,g24)
    c: Equal(g24,g25)
    c: Equal(g25,g26)
    c: Equal(g26,g27)
    c: Equal(g27,g28)
    c: Coincident(g29,g18)
    c: Coincident(g4,g18)
    c: PointOnObject(g8,g9)
    c: Tangent(g0,g31) = 1.5708
    c: Tangent(g5,g31) = 1.5708
    c: DistanceY(g0,g5) = 1.5
    c: Radius(g31) = 0.1
FEATURE [PartDesign::Revolution] Revolution
  Angle = 360
  Axis = (-2e-16,3e-16,1)
  Base = (0,0,0)
  Placement = pos=(0,0,0) rot=(0.57735,0.57735,0.57735;2.0944rad)
  Profile = -> Sketch002
  ReferenceAxis = -> Sketch002 [V_Axis]
FEATURE [PartDesign::Body] Body  label="center"
  Group = -> [Sketch002,Revolution]
  Origin = -> Origin001
  Tip = -> Revolution
FEATURE [Part::Fuse] Fusion
  Base = -> Body
  Tool = -> Body001
FEATURE [PartDesign::CoordinateSystem] LCS_topcenter
  AttacherType = Attacher::AttachEngine3D
  MapMode = 5
  Placement = pos=(-8e-16,5e-16,1.4) rot=(0,0,1;0rad)
  Support = -> [Fusion]
  expr: .AttachmentOffset.Base.z = -master_animator#Variables.explode * 7
FEATURE [App::Part] Part  label="hand_seconds"
  Group = -> [Body,Body001,Fusion,LCS_topcenter]
  Origin = -> Origin
